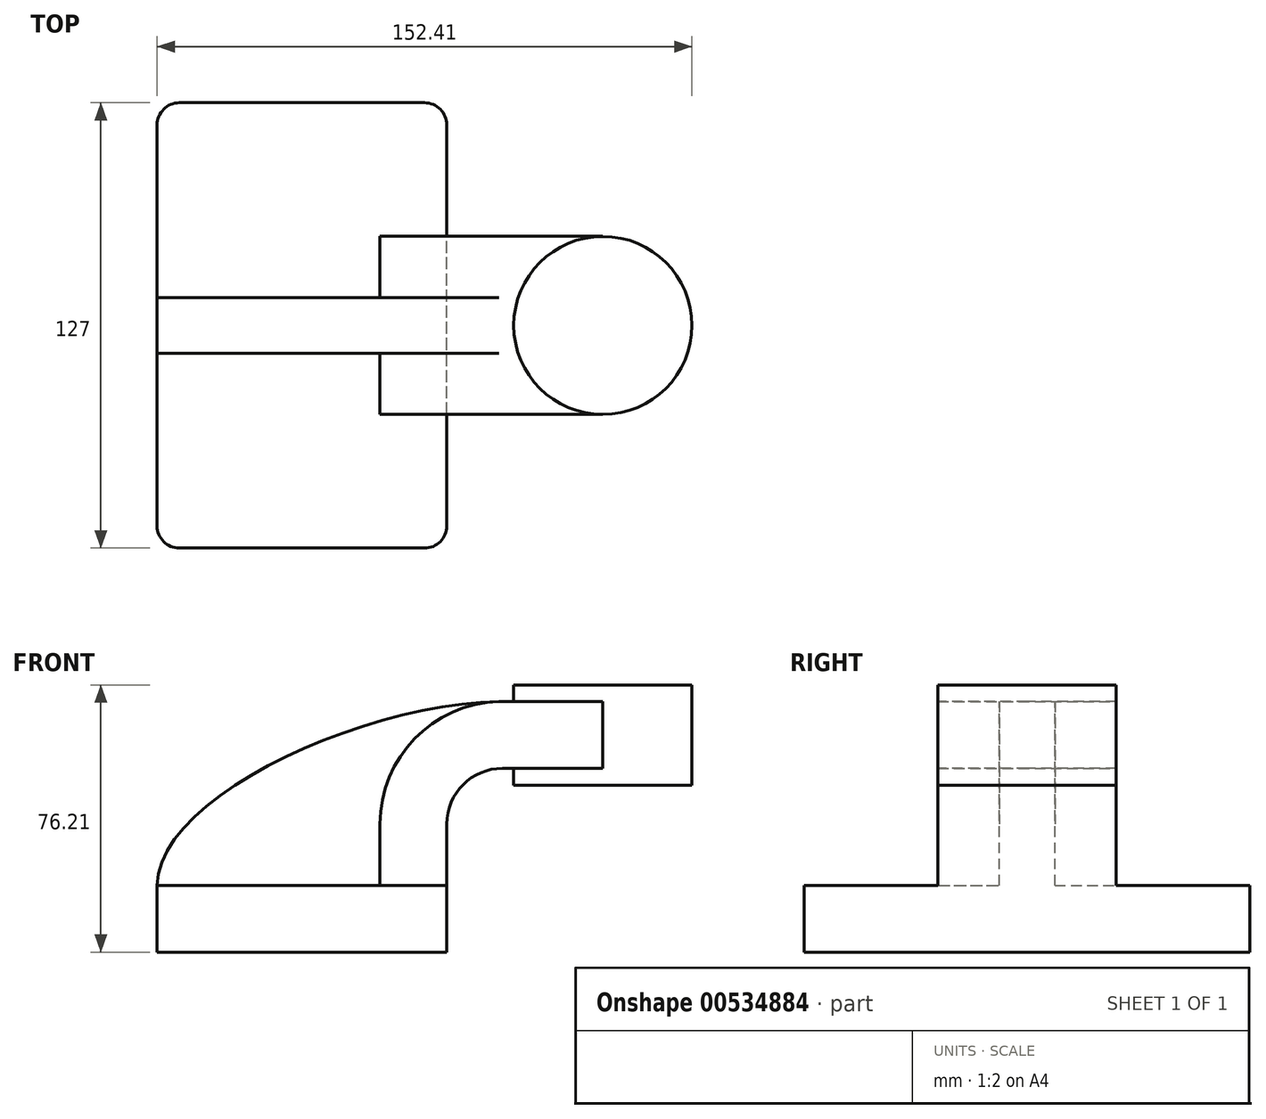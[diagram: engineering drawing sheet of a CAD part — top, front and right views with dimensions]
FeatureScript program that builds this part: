
annotation { "Feature Type Name" : "Feature", "Feature Type Description" : "" }
export const myFeature = defineFeature(function(context is Context, id is Id, definition is map)
    precondition{}
    {
        {
            var Q0;
            Q0=qCreatedBy(makeId("Front.planeOp"),FACE);
            var sketch = newSketch(context, id + "F0", { "sketchPlane" : qUnion([Q0])});
            skLineSegment(sketch, "E0.bottom", {"start": v(41.28, -9.52) * mm, "end": v(-41.28, -9.53) * mm});
            skLineSegment(sketch, "E0.top", {"start": v(41.28, 9.53) * mm, "end": v(-41.28, 9.52) * mm});
            skLineSegment(sketch, "E0.left", {"start": v(41.28, -9.52) * mm, "end": v(41.28, 9.53) * mm});
            skLineSegment(sketch, "E0.right", {"start": v(-41.28, -9.53) * mm, "end": v(-41.28, 9.52) * mm});
            skPoint(sketch, "E0.middle", {"position": v(0, 0) * mm});
            skLineSegment(sketch, "E1.bottom", {"start": v(111.12, 38.1) * mm, "end": v(60.32, 38.1) * mm});
            skLineSegment(sketch, "E1.top", {"start": v(111.12, 66.68) * mm, "end": v(60.32, 66.68) * mm});
            skLineSegment(sketch, "E1.left", {"start": v(111.12, 38.1) * mm, "end": v(111.12, 66.68) * mm});
            skLineSegment(sketch, "E1.right", {"start": v(60.32, 38.1) * mm, "end": v(60.32, 66.68) * mm});
            skPoint(sketch, "E1.middle", {"position": v(85.72, 52.39) * mm});
            skLineSegment(sketch, "E2", {"start": v(41.28, 9.53) * mm, "end": v(41.28, 27) * mm});
            skArc(sketch, "E3", {"start": v(41.28, 27) * mm, "mid": v(45.92, 38.23) * mm, "end": v(57.15, 42.88) * mm});
            skLineSegment(sketch, "E4", {"start": v(57.15, 42.88) * mm, "end": v(85.74, 42.88) * mm});
            skLineSegment(sketch, "E5.0", {"start": v(57.15, 61.93) * mm, "end": v(85.74, 61.93) * mm});
            skArc(sketch, "E5.1", {"start": v(22.23, 27) * mm, "mid": v(32.45, 51.7) * mm, "end": v(57.15, 61.93) * mm});
            skLineSegment(sketch, "E5.2", {"start": v(22.23, 9.53) * mm, "end": v(22.23, 27) * mm});
            skLineSegment(sketch, "E6", {"start": v(85.74, 42.88) * mm, "end": v(85.74, 66.68) * mm});
            skFitSpline(sketch, "E7", {"points": [v(-41.28, 9.52) * mm, v(57.15, 61.93) * mm], "startDerivative": vector(0.54, 76.4) * mm, "endDerivative": vector(117.64, 1.03) * mm});
            skLineSegment(sketch, "E8", {"start": v(85.74, 42.88) * mm, "end": v(85.74, 38.1) * mm});
            skSolve(sketch);
        }
        {
            var Q0;
            Q0=makeQuery(id+"F0.imprint","IMPRINT",FACE,{"disambiguationData":[TD([[makeQuery(id+"F0.imprint","IMPRINT",EDGE,{"derivedFrom":sQuery(id+"F0.wireOp",EDGE,"E0.bottom")}),-1.0]])]});
            extrude(context, id + "F1", {"entities" : qUnion([Q0]), "endBound" : BoundingType.SYMMETRIC, "depth" : 127 * mm, "offsetDistance" : 25.4 * mm});
        }
        {
            var Q0;
            {var subQ6=sQuery(id+"F0.wireOp",EDGE,"E2");Q0=makeQuery(id+"F0.imprint","IMPRINT",FACE,{"disambiguationData":[TD([[makeQuery(id+"F0.imprint","IMPRINT",EDGE,{"derivedFrom":subQ6}),1.0]])]});}
            var Q1;
            {var subQ0=sQuery(id+"F0.wireOp",EDGE,"E4");var subQ1=sQuery(id+"F0.wireOp",EDGE,"E1.right");var subQ2=makeQuery(id+"F0.imprint","INTERSECT",VERTEX,{"derivedFrom":[subQ1,subQ0]});Q1=makeQuery(id+"F0.imprint","IMPRINT",FACE,{"disambiguationData":[TD([[makeQuery(id+"F0.imprint","IMPRINT",EDGE,{"disambiguationData":[TD([[subQ2,-1.0]])],"derivedFrom":subQ1}),-1.0]])]});}
            extrude(context, id + "F2", {"entities" : qUnion([Q0, Q1]), "operationType" : NewBodyOperationType.ADD, "endBound" : BoundingType.SYMMETRIC, "depth" : 50.8 * mm, "offsetDistance" : 25.4 * mm});
        }
        {
            var Q0;
            {var subQ3=sQuery(id+"F0.wireOp",EDGE,"E5.2");Q0=makeQuery(id+"F0.imprint","IMPRINT",FACE,{"disambiguationData":[TD([[makeQuery(id+"F0.imprint","IMPRINT",EDGE,{"derivedFrom":subQ3}),1.0]])]});}
            extrude(context, id + "F3", {"entities" : qUnion([Q0]), "operationType" : NewBodyOperationType.ADD, "endBound" : BoundingType.SYMMETRIC, "depth" : 15.88 * mm, "offsetDistance" : 25.4 * mm});
        }
        {
            var Q0;
            {var subQ0=sQuery(id+"F0.wireOp",EDGE,"E1.left");Q0=makeQuery(id+"F0.imprint","IMPRINT",FACE,{"disambiguationData":[TD([[makeQuery(id+"F0.imprint","IMPRINT",EDGE,{"derivedFrom":subQ0}),1.0]])]});}
            var Q1;
            Q1=sQuery(id+"F0.wireOp",EDGE,"E6");
            revolve(context, id + "F4", {"operationType" : NewBodyOperationType.ADD, "entities" : qUnion([Q0]), "axis" : qUnion([Q1]), "revolveType" : RevolveType.FULL});
        }
        {
            var Q0;
            Q0=makeQuery(id+"F1.opExtrude","CAP_EDGE",EDGE,{"disambiguationData":[OSD([sQuery(id+"F0.wireOp",EDGE,"E0.right")])],"isStart":false});
            var Q1;
            Q1=makeQuery(id+"F1.opExtrude","CAP_EDGE",EDGE,{"disambiguationData":[OSD([sQuery(id+"F0.wireOp",EDGE,"E0.left")])],"isStart":false});
            var Q2;
            Q2=makeQuery(id+"F1.opExtrude","CAP_EDGE",EDGE,{"disambiguationData":[OSD([sQuery(id+"F0.wireOp",EDGE,"E0.left")])],"isStart":true});
            var Q3;
            Q3=makeQuery(id+"F1.opExtrude","CAP_EDGE",EDGE,{"disambiguationData":[OSD([sQuery(id+"F0.wireOp",EDGE,"E0.right")])],"isStart":true});
            fillet(context, id + "F5", {"entities" : qUnion([Q0, Q1, Q2, Q3]), "radius" : 6.35 * mm, "tangentPropagation" : true, "allowEdgeOverflow" : false});
        }
    });
